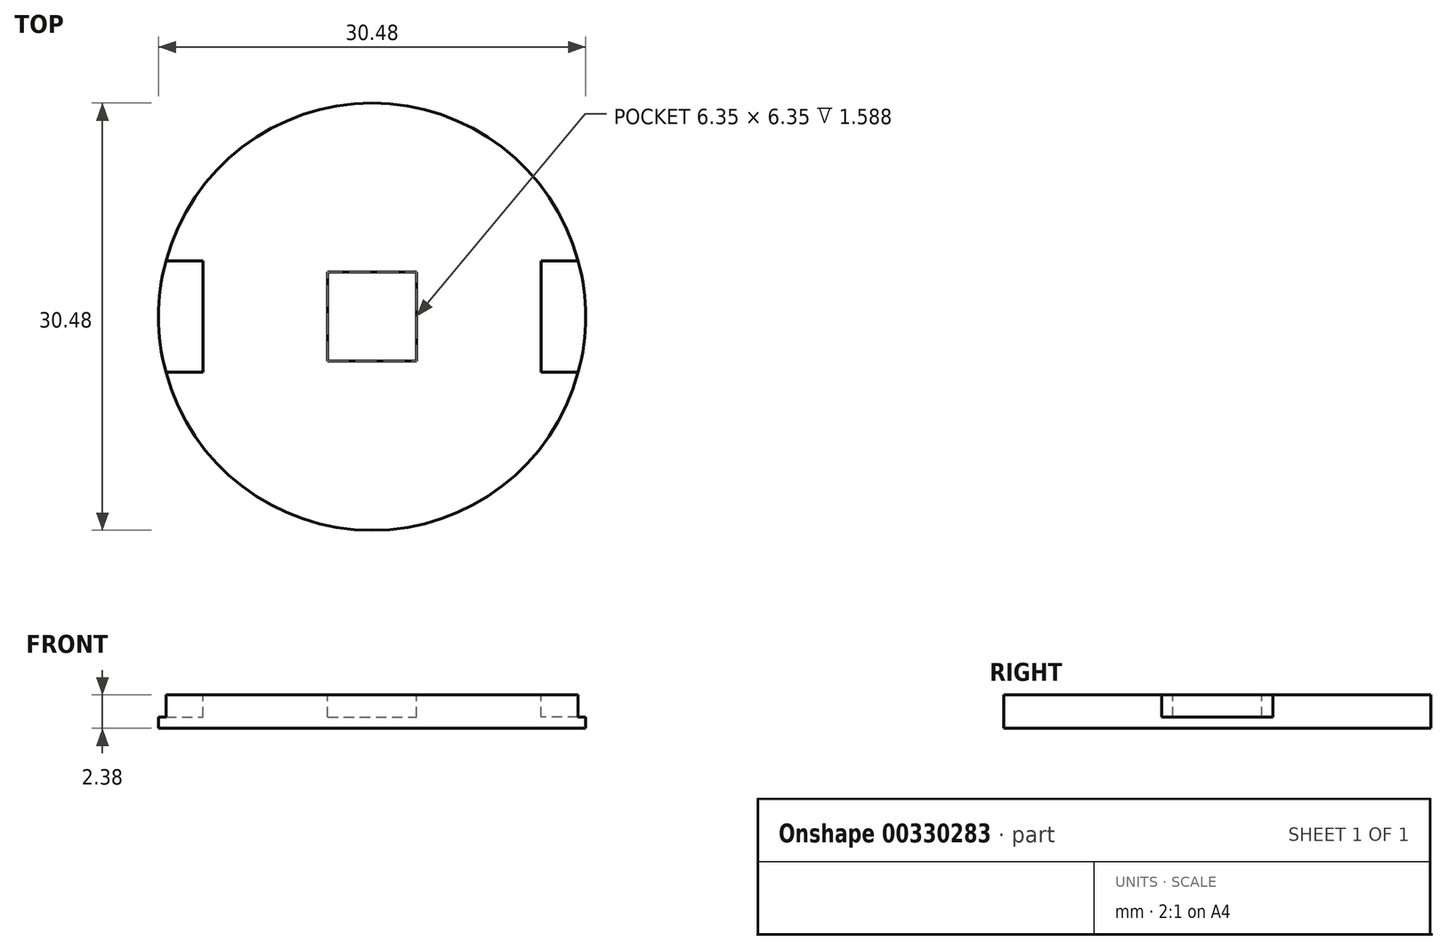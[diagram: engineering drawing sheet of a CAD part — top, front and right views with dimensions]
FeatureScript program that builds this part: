
annotation { "Feature Type Name" : "Feature", "Feature Type Description" : "" }
export const myFeature = defineFeature(function(context is Context, id is Id, definition is map)
    precondition{}
    {
        {
            var Q0;
            Q0=qCreatedBy(makeId("Top.planeOp"),FACE);
            var sketch = newSketch(context, id + "F0", { "sketchPlane" : qUnion([Q0])});
            skEllipse(sketch, "E0", {"center": v(0, 0) * mm, "majorRadius": 15.24 * mm, "minorRadius": 15.24 * mm, "majorAxis": v(0, 1)});
            skSolve(sketch);
        }
        {
            var Q0;
            Q0 = qSketchRegion(id + "F0", true);
            extrude(context, id + "F1", {"entities" : qUnion([Q0]), "depth" : 2.38 * mm});
        }
        {
            var Q0;
            Q0=qCreatedBy(makeId("Right.planeOp"),FACE);
            var sketch = newSketch(context, id + "F2", { "sketchPlane" : qUnion([Q0])});
            skLineSegment(sketch, "E1", {"start": v(0, 0.8) * mm, "end": v(-3.18, 0.8) * mm});
            skLineSegment(sketch, "E2", {"start": v(-3.18, 0.8) * mm, "end": v(-3.18, 3.94) * mm});
            skLineSegment(sketch, "E3.MirrorCS", {"start": v(3.18, 0.8) * mm, "end": v(3.18, 3.94) * mm});
            skLineSegment(sketch, "E4.MirrorCS", {"start": v(0, 0.8) * mm, "end": v(3.18, 0.8) * mm});
            skLineSegment(sketch, "E5", {"start": v(3.18, 3.94) * mm, "end": v(-3.18, 3.94) * mm});
            skSolve(sketch);
        }
        {
            var Q0;
            Q0 = qSketchRegion(id + "F2", true);
            extrude(context, id + "F3", {"entities" : qUnion([Q0]), "operationType" : NewBodyOperationType.REMOVE, "oppositeDirection" : true, "depth" : 6.35 * mm, "symmetric" : true});
        }
        {
            var Q0;
            Q0=makeQuery(id+"F1.opExtrude","CAP_FACE",FACE,{"disambiguationData":[OSD([sQuery(id+"F0.wireOp",EDGE,"E0")])],"isStart":false});
            var sketch = newSketch(context, id + "F4", { "sketchPlane" : qUnion([Q0])});
            skLineSegment(sketch, "E6.bottom", {"start": v(-15.24, 3.97) * mm, "end": v(-12.06, 3.97) * mm});
            skLineSegment(sketch, "E6.top", {"start": v(-15.24, -3.97) * mm, "end": v(-12.06, -3.97) * mm});
            skLineSegment(sketch, "E6.left", {"start": v(-15.24, 3.97) * mm, "end": v(-15.24, -3.97) * mm});
            skLineSegment(sketch, "E6.right", {"start": v(-12.06, 3.97) * mm, "end": v(-12.06, -3.97) * mm});
            skLineSegment(sketch, "E7.MirrorCS", {"start": v(12.06, 3.97) * mm, "end": v(12.06, -3.97) * mm});
            skLineSegment(sketch, "E8.MirrorCS", {"start": v(15.24, 3.97) * mm, "end": v(15.24, -3.97) * mm});
            skLineSegment(sketch, "E9.MirrorCS", {"start": v(15.24, 3.97) * mm, "end": v(12.06, 3.97) * mm});
            skLineSegment(sketch, "E10.MirrorCS", {"start": v(15.24, -3.97) * mm, "end": v(12.06, -3.97) * mm});
            skSolve(sketch);
        }
        {
            var Q0;
            Q0 = qSketchRegion(id + "F4", true);
            extrude(context, id + "F5", {"entities" : qUnion([Q0]), "operationType" : NewBodyOperationType.REMOVE, "oppositeDirection" : true, "depth" : 1.59 * mm});
        }
    });
